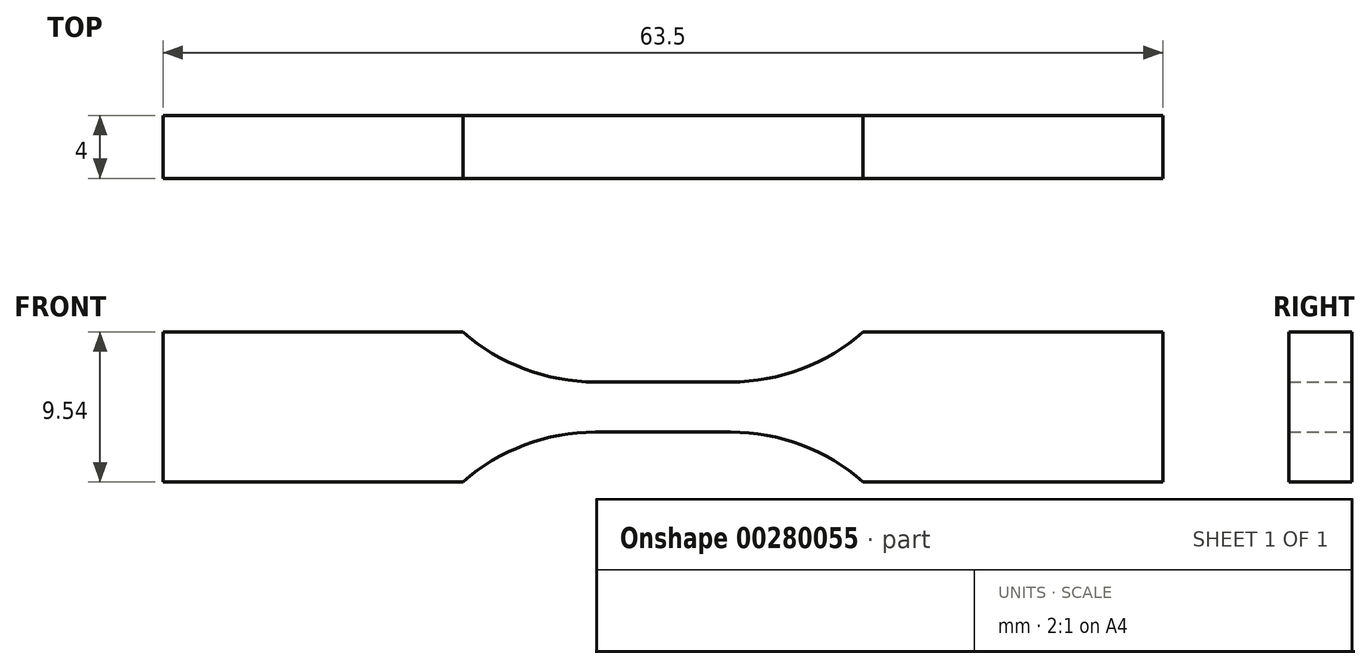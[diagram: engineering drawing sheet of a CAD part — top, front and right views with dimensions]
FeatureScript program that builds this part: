
annotation { "Feature Type Name" : "Feature", "Feature Type Description" : "" }
export const myFeature = defineFeature(function(context is Context, id is Id, definition is map)
    precondition{}
    {
        {
            var Q0;
            Q0=qCreatedBy(makeId("Front.planeOp"),FACE);
            var sketch = newSketch(context, id + "F0", { "sketchPlane" : qUnion([Q0])});
            skLineSegment(sketch, "E0", {"start": v(0, 1.6) * mm, "end": v(4.3, 1.6) * mm});
            skArc(sketch, "E1", {"start": v(4.3, 1.6) * mm, "mid": v(8.79, 2.41) * mm, "end": v(12.7, 4.76) * mm});
            skLineSegment(sketch, "E2", {"start": v(12.7, 4.77) * mm, "end": v(31.75, 4.77) * mm});
            skLineSegment(sketch, "E3", {"start": v(31.75, 4.77) * mm, "end": v(31.75, 0) * mm});
            skLineSegment(sketch, "E4.MirrorCS", {"start": v(0, -1.6) * mm, "end": v(4.3, -1.6) * mm});
            skLineSegment(sketch, "E5.MirrorCS", {"start": v(31.75, -4.77) * mm, "end": v(31.75, 0) * mm});
            skLineSegment(sketch, "E6.MirrorCS", {"start": v(12.7, -4.77) * mm, "end": v(31.75, -4.77) * mm});
            skArc(sketch, "E7.MirrorCS", {"start": v(4.3, -1.6) * mm, "mid": v(8.79, -2.41) * mm, "end": v(12.7, -4.76) * mm});
            skArc(sketch, "E8.MirrorCS", {"start": v(-4.3, -1.6) * mm, "mid": v(-8.79, -2.41) * mm, "end": v(-12.7, -4.76) * mm});
            skLineSegment(sketch, "E9.MirrorCS", {"start": v(-12.7, -4.77) * mm, "end": v(-31.75, -4.77) * mm});
            skLineSegment(sketch, "E10.MirrorCS", {"start": v(0, 1.6) * mm, "end": v(-4.3, 1.6) * mm});
            skArc(sketch, "E11.MirrorCS", {"start": v(-4.3, 1.6) * mm, "mid": v(-8.79, 2.41) * mm, "end": v(-12.7, 4.76) * mm});
            skLineSegment(sketch, "E12.MirrorCS", {"start": v(-12.7, 4.77) * mm, "end": v(-31.75, 4.76) * mm});
            skLineSegment(sketch, "E13.MirrorCS", {"start": v(-31.75, -4.77) * mm, "end": v(-31.75, 0) * mm});
            skLineSegment(sketch, "E14.MirrorCS", {"start": v(-31.75, 4.77) * mm, "end": v(-31.75, 0) * mm});
            skLineSegment(sketch, "E15.MirrorCS", {"start": v(0, -1.59) * mm, "end": v(-4.3, -1.59) * mm});
            skSolve(sketch);
        }
        {
            var Q0;
            Q0 = qSketchRegion(id + "F0", true);
            extrude(context, id + "F1", {"entities" : qUnion([Q0]), "endBound" : BoundingType.SYMMETRIC, "depth" : 4 * mm});
        }
    });
